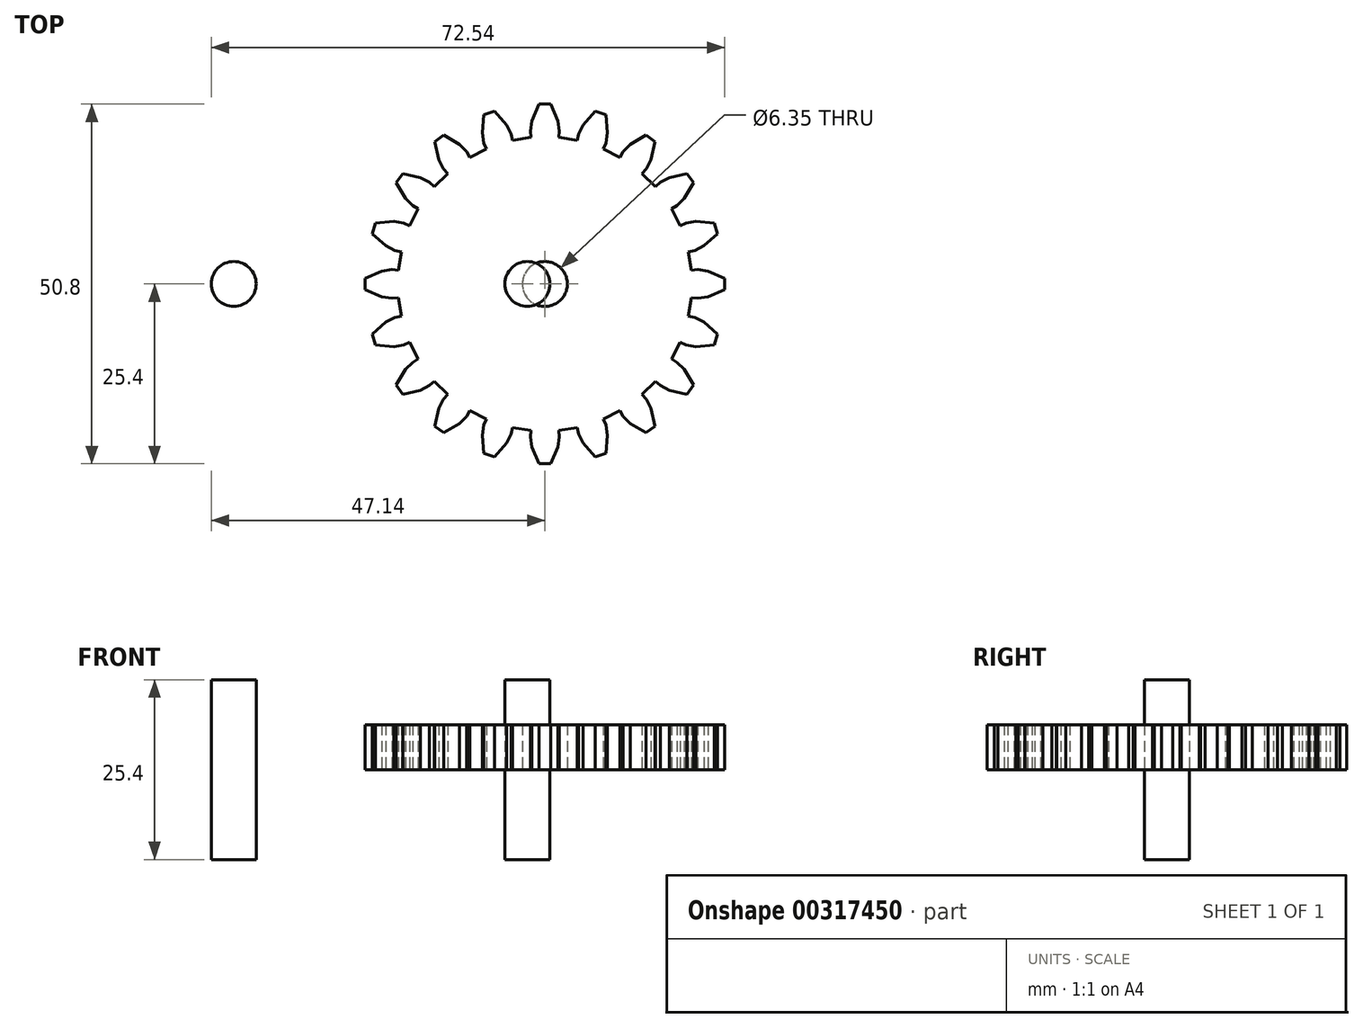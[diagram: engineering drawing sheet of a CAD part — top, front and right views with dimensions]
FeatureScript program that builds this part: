
annotation { "Feature Type Name" : "Feature", "Feature Type Description" : "" }
export const myFeature = defineFeature(function(context is Context, id is Id, definition is map)
    precondition{}
    {
        {
            var Q0;
            Q0=qCreatedBy(makeId("Top.planeOp"),FACE);
            var sketch = newSketch(context, id + "F0", { "sketchPlane" : qUnion([Q0])});
            skLineSegment(sketch, "E0", {"start": v(20.7, 1.94) * mm, "end": v(21.61, 2.03) * mm});
            skLineSegment(sketch, "E1", {"start": v(21.61, 2.03) * mm, "end": v(23.03, 1.81) * mm});
            skLineSegment(sketch, "E2", {"start": v(23.03, 1.81) * mm, "end": v(25.4, 0.8) * mm});
            skLineSegment(sketch, "E3", {"start": v(25.4, 0.8) * mm, "end": v(25.4, -0.8) * mm});
            skLineSegment(sketch, "E4", {"start": v(25.4, -0.8) * mm, "end": v(23.03, -1.81) * mm});
            skLineSegment(sketch, "E5", {"start": v(23.03, -1.81) * mm, "end": v(21.61, -2.03) * mm});
            skLineSegment(sketch, "E6", {"start": v(21.61, -2.03) * mm, "end": v(20.7, -1.94) * mm});
            skLineSegment(sketch, "E7", {"start": v(20.7, -1.94) * mm, "end": v(20.29, -4.55) * mm});
            skLineSegment(sketch, "E8", {"start": v(20.29, -4.55) * mm, "end": v(21.18, -4.75) * mm});
            skLineSegment(sketch, "E9", {"start": v(21.18, -4.75) * mm, "end": v(22.46, -5.4) * mm});
            skLineSegment(sketch, "E10", {"start": v(22.46, -5.4) * mm, "end": v(24.4, -7.09) * mm});
            skLineSegment(sketch, "E11", {"start": v(24.4, -7.09) * mm, "end": v(23.9, -8.61) * mm});
            skLineSegment(sketch, "E12", {"start": v(23.9, -8.61) * mm, "end": v(21.34, -8.84) * mm});
            skLineSegment(sketch, "E13", {"start": v(21.34, -8.84) * mm, "end": v(19.93, -8.6) * mm});
            skLineSegment(sketch, "E14", {"start": v(19.93, -8.6) * mm, "end": v(19.09, -8.24) * mm});
            skLineSegment(sketch, "E15", {"start": v(19.09, -8.24) * mm, "end": v(17.89, -10.6) * mm});
            skLineSegment(sketch, "E16", {"start": v(17.89, -10.6) * mm, "end": v(18.68, -11.07) * mm});
            skLineSegment(sketch, "E17", {"start": v(18.68, -11.07) * mm, "end": v(19.7, -12.07) * mm});
            skLineSegment(sketch, "E18", {"start": v(19.7, -12.07) * mm, "end": v(21.02, -14.28) * mm});
            skLineSegment(sketch, "E19", {"start": v(21.02, -14.28) * mm, "end": v(20.08, -15.58) * mm});
            skLineSegment(sketch, "E20", {"start": v(20.08, -15.58) * mm, "end": v(17.57, -15) * mm});
            skLineSegment(sketch, "E21", {"start": v(17.57, -15) * mm, "end": v(16.3, -14.34) * mm});
            skLineSegment(sketch, "E22", {"start": v(16.3, -14.34) * mm, "end": v(15.6, -13.74) * mm});
            skLineSegment(sketch, "E23", {"start": v(15.6, -13.74) * mm, "end": v(13.74, -15.6) * mm});
            skLineSegment(sketch, "E24", {"start": v(13.74, -15.6) * mm, "end": v(14.34, -16.3) * mm});
            skLineSegment(sketch, "E25", {"start": v(14.34, -16.3) * mm, "end": v(15, -17.57) * mm});
            skLineSegment(sketch, "E26", {"start": v(15, -17.57) * mm, "end": v(15.58, -20.08) * mm});
            skLineSegment(sketch, "E27", {"start": v(15.58, -20.08) * mm, "end": v(14.28, -21.02) * mm});
            skLineSegment(sketch, "E28", {"start": v(14.28, -21.02) * mm, "end": v(12.07, -19.7) * mm});
            skLineSegment(sketch, "E29", {"start": v(12.07, -19.7) * mm, "end": v(11.07, -18.68) * mm});
            skLineSegment(sketch, "E30", {"start": v(11.07, -18.68) * mm, "end": v(10.6, -17.89) * mm});
            skLineSegment(sketch, "E31", {"start": v(10.6, -17.89) * mm, "end": v(8.24, -19.09) * mm});
            skLineSegment(sketch, "E32", {"start": v(8.24, -19.09) * mm, "end": v(8.6, -19.93) * mm});
            skLineSegment(sketch, "E33", {"start": v(8.6, -19.93) * mm, "end": v(8.84, -21.34) * mm});
            skLineSegment(sketch, "E34", {"start": v(8.84, -21.34) * mm, "end": v(8.61, -23.9) * mm});
            skLineSegment(sketch, "E35", {"start": v(8.61, -23.9) * mm, "end": v(7.09, -24.4) * mm});
            skLineSegment(sketch, "E36", {"start": v(7.09, -24.4) * mm, "end": v(5.4, -22.46) * mm});
            skLineSegment(sketch, "E37", {"start": v(5.4, -22.46) * mm, "end": v(4.75, -21.18) * mm});
            skLineSegment(sketch, "E38", {"start": v(4.75, -21.18) * mm, "end": v(4.55, -20.29) * mm});
            skLineSegment(sketch, "E39", {"start": v(4.55, -20.29) * mm, "end": v(1.94, -20.7) * mm});
            skLineSegment(sketch, "E40", {"start": v(1.94, -20.7) * mm, "end": v(2.03, -21.61) * mm});
            skLineSegment(sketch, "E41", {"start": v(2.03, -21.61) * mm, "end": v(1.81, -23.03) * mm});
            skLineSegment(sketch, "E42", {"start": v(1.81, -23.03) * mm, "end": v(0.8, -25.4) * mm});
            skLineSegment(sketch, "E43", {"start": v(0.8, -25.4) * mm, "end": v(-0.8, -25.4) * mm});
            skLineSegment(sketch, "E44", {"start": v(-0.8, -25.4) * mm, "end": v(-1.81, -23.03) * mm});
            skLineSegment(sketch, "E45", {"start": v(-1.81, -23.03) * mm, "end": v(-2.03, -21.61) * mm});
            skLineSegment(sketch, "E46", {"start": v(-2.03, -21.61) * mm, "end": v(-1.94, -20.7) * mm});
            skLineSegment(sketch, "E47", {"start": v(-1.94, -20.7) * mm, "end": v(-4.55, -20.29) * mm});
            skLineSegment(sketch, "E48", {"start": v(-4.55, -20.29) * mm, "end": v(-4.75, -21.18) * mm});
            skLineSegment(sketch, "E49", {"start": v(-4.75, -21.18) * mm, "end": v(-5.4, -22.46) * mm});
            skLineSegment(sketch, "E50", {"start": v(-5.4, -22.46) * mm, "end": v(-7.09, -24.4) * mm});
            skLineSegment(sketch, "E51", {"start": v(-7.09, -24.4) * mm, "end": v(-8.61, -23.9) * mm});
            skLineSegment(sketch, "E52", {"start": v(-8.61, -23.9) * mm, "end": v(-8.84, -21.34) * mm});
            skLineSegment(sketch, "E53", {"start": v(-8.84, -21.34) * mm, "end": v(-8.6, -19.93) * mm});
            skLineSegment(sketch, "E54", {"start": v(-8.6, -19.93) * mm, "end": v(-8.24, -19.09) * mm});
            skLineSegment(sketch, "E55", {"start": v(-8.24, -19.09) * mm, "end": v(-10.6, -17.89) * mm});
            skLineSegment(sketch, "E56", {"start": v(-10.6, -17.89) * mm, "end": v(-11.07, -18.68) * mm});
            skLineSegment(sketch, "E57", {"start": v(-11.07, -18.68) * mm, "end": v(-12.07, -19.7) * mm});
            skLineSegment(sketch, "E58", {"start": v(-12.07, -19.7) * mm, "end": v(-14.28, -21.02) * mm});
            skLineSegment(sketch, "E59", {"start": v(-14.28, -21.02) * mm, "end": v(-15.58, -20.08) * mm});
            skLineSegment(sketch, "E60", {"start": v(-15.58, -20.08) * mm, "end": v(-15, -17.57) * mm});
            skLineSegment(sketch, "E61", {"start": v(-15, -17.57) * mm, "end": v(-14.34, -16.3) * mm});
            skLineSegment(sketch, "E62", {"start": v(-14.34, -16.3) * mm, "end": v(-13.74, -15.6) * mm});
            skLineSegment(sketch, "E63", {"start": v(-13.74, -15.6) * mm, "end": v(-15.6, -13.74) * mm});
            skLineSegment(sketch, "E64", {"start": v(-15.6, -13.74) * mm, "end": v(-16.3, -14.34) * mm});
            skLineSegment(sketch, "E65", {"start": v(-16.3, -14.34) * mm, "end": v(-17.57, -15) * mm});
            skLineSegment(sketch, "E66", {"start": v(-17.57, -15) * mm, "end": v(-20.08, -15.58) * mm});
            skLineSegment(sketch, "E67", {"start": v(-20.08, -15.58) * mm, "end": v(-21.02, -14.28) * mm});
            skLineSegment(sketch, "E68", {"start": v(-21.02, -14.28) * mm, "end": v(-19.7, -12.07) * mm});
            skLineSegment(sketch, "E69", {"start": v(-19.7, -12.07) * mm, "end": v(-18.68, -11.07) * mm});
            skLineSegment(sketch, "E70", {"start": v(-18.68, -11.07) * mm, "end": v(-17.89, -10.6) * mm});
            skLineSegment(sketch, "E71", {"start": v(-17.89, -10.6) * mm, "end": v(-19.09, -8.24) * mm});
            skLineSegment(sketch, "E72", {"start": v(-19.09, -8.24) * mm, "end": v(-19.93, -8.6) * mm});
            skLineSegment(sketch, "E73", {"start": v(-19.93, -8.6) * mm, "end": v(-21.34, -8.84) * mm});
            skLineSegment(sketch, "E74", {"start": v(-21.34, -8.84) * mm, "end": v(-23.9, -8.61) * mm});
            skLineSegment(sketch, "E75", {"start": v(-23.9, -8.61) * mm, "end": v(-24.4, -7.09) * mm});
            skLineSegment(sketch, "E76", {"start": v(-24.4, -7.09) * mm, "end": v(-22.46, -5.4) * mm});
            skLineSegment(sketch, "E77", {"start": v(-22.46, -5.4) * mm, "end": v(-21.18, -4.75) * mm});
            skLineSegment(sketch, "E78", {"start": v(-21.18, -4.75) * mm, "end": v(-20.29, -4.55) * mm});
            skLineSegment(sketch, "E79", {"start": v(-20.29, -4.55) * mm, "end": v(-20.7, -1.94) * mm});
            skLineSegment(sketch, "E80", {"start": v(-20.7, -1.94) * mm, "end": v(-21.61, -2.03) * mm});
            skLineSegment(sketch, "E81", {"start": v(-21.61, -2.03) * mm, "end": v(-23.03, -1.81) * mm});
            skLineSegment(sketch, "E82", {"start": v(-23.03, -1.81) * mm, "end": v(-25.4, -0.8) * mm});
            skLineSegment(sketch, "E83", {"start": v(-25.4, -0.8) * mm, "end": v(-25.4, 0.8) * mm});
            skLineSegment(sketch, "E84", {"start": v(-25.4, 0.8) * mm, "end": v(-23.03, 1.81) * mm});
            skLineSegment(sketch, "E85", {"start": v(-23.03, 1.81) * mm, "end": v(-21.61, 2.03) * mm});
            skLineSegment(sketch, "E86", {"start": v(-21.61, 2.03) * mm, "end": v(-20.7, 1.94) * mm});
            skLineSegment(sketch, "E87", {"start": v(-20.7, 1.94) * mm, "end": v(-20.29, 4.55) * mm});
            skLineSegment(sketch, "E88", {"start": v(-20.29, 4.55) * mm, "end": v(-21.18, 4.75) * mm});
            skLineSegment(sketch, "E89", {"start": v(-21.18, 4.75) * mm, "end": v(-22.46, 5.4) * mm});
            skLineSegment(sketch, "E90", {"start": v(-22.46, 5.4) * mm, "end": v(-24.4, 7.09) * mm});
            skLineSegment(sketch, "E91", {"start": v(-24.4, 7.09) * mm, "end": v(-23.9, 8.61) * mm});
            skLineSegment(sketch, "E92", {"start": v(-23.9, 8.61) * mm, "end": v(-21.34, 8.84) * mm});
            skLineSegment(sketch, "E93", {"start": v(-21.34, 8.84) * mm, "end": v(-19.93, 8.6) * mm});
            skLineSegment(sketch, "E94", {"start": v(-19.93, 8.6) * mm, "end": v(-19.09, 8.24) * mm});
            skLineSegment(sketch, "E95", {"start": v(-19.09, 8.24) * mm, "end": v(-17.89, 10.6) * mm});
            skLineSegment(sketch, "E96", {"start": v(-17.89, 10.6) * mm, "end": v(-18.68, 11.07) * mm});
            skLineSegment(sketch, "E97", {"start": v(-18.68, 11.07) * mm, "end": v(-19.7, 12.07) * mm});
            skLineSegment(sketch, "E98", {"start": v(-19.7, 12.07) * mm, "end": v(-21.02, 14.28) * mm});
            skLineSegment(sketch, "E99", {"start": v(-21.02, 14.28) * mm, "end": v(-20.08, 15.58) * mm});
            skLineSegment(sketch, "E100", {"start": v(-20.08, 15.58) * mm, "end": v(-17.57, 15) * mm});
            skLineSegment(sketch, "E101", {"start": v(-17.57, 15) * mm, "end": v(-16.3, 14.34) * mm});
            skLineSegment(sketch, "E102", {"start": v(-16.3, 14.34) * mm, "end": v(-15.6, 13.74) * mm});
            skLineSegment(sketch, "E103", {"start": v(-15.6, 13.74) * mm, "end": v(-13.74, 15.6) * mm});
            skLineSegment(sketch, "E104", {"start": v(-13.74, 15.6) * mm, "end": v(-14.34, 16.3) * mm});
            skLineSegment(sketch, "E105", {"start": v(-14.34, 16.3) * mm, "end": v(-15, 17.57) * mm});
            skLineSegment(sketch, "E106", {"start": v(-15, 17.57) * mm, "end": v(-15.58, 20.08) * mm});
            skLineSegment(sketch, "E107", {"start": v(-15.58, 20.08) * mm, "end": v(-14.28, 21.02) * mm});
            skLineSegment(sketch, "E108", {"start": v(-14.28, 21.02) * mm, "end": v(-12.07, 19.7) * mm});
            skLineSegment(sketch, "E109", {"start": v(-12.07, 19.7) * mm, "end": v(-11.07, 18.68) * mm});
            skLineSegment(sketch, "E110", {"start": v(-11.07, 18.68) * mm, "end": v(-10.6, 17.89) * mm});
            skLineSegment(sketch, "E111", {"start": v(-10.6, 17.89) * mm, "end": v(-8.24, 19.09) * mm});
            skLineSegment(sketch, "E112", {"start": v(-8.24, 19.09) * mm, "end": v(-8.6, 19.93) * mm});
            skLineSegment(sketch, "E113", {"start": v(-8.6, 19.93) * mm, "end": v(-8.84, 21.34) * mm});
            skLineSegment(sketch, "E114", {"start": v(-8.84, 21.34) * mm, "end": v(-8.61, 23.9) * mm});
            skLineSegment(sketch, "E115", {"start": v(-8.61, 23.9) * mm, "end": v(-7.09, 24.4) * mm});
            skLineSegment(sketch, "E116", {"start": v(-7.09, 24.4) * mm, "end": v(-5.4, 22.46) * mm});
            skLineSegment(sketch, "E117", {"start": v(-5.4, 22.46) * mm, "end": v(-4.75, 21.18) * mm});
            skLineSegment(sketch, "E118", {"start": v(-4.75, 21.18) * mm, "end": v(-4.55, 20.29) * mm});
            skLineSegment(sketch, "E119", {"start": v(-4.55, 20.29) * mm, "end": v(-1.94, 20.7) * mm});
            skLineSegment(sketch, "E120", {"start": v(-1.94, 20.7) * mm, "end": v(-2.03, 21.61) * mm});
            skLineSegment(sketch, "E121", {"start": v(-2.03, 21.61) * mm, "end": v(-1.81, 23.03) * mm});
            skLineSegment(sketch, "E122", {"start": v(-1.81, 23.03) * mm, "end": v(-0.8, 25.4) * mm});
            skLineSegment(sketch, "E123", {"start": v(-0.8, 25.4) * mm, "end": v(0.8, 25.4) * mm});
            skLineSegment(sketch, "E124", {"start": v(0.8, 25.4) * mm, "end": v(1.81, 23.03) * mm});
            skLineSegment(sketch, "E125", {"start": v(1.81, 23.03) * mm, "end": v(2.03, 21.61) * mm});
            skLineSegment(sketch, "E126", {"start": v(2.03, 21.61) * mm, "end": v(1.94, 20.7) * mm});
            skLineSegment(sketch, "E127", {"start": v(1.94, 20.7) * mm, "end": v(4.55, 20.29) * mm});
            skLineSegment(sketch, "E128", {"start": v(4.55, 20.29) * mm, "end": v(4.75, 21.18) * mm});
            skLineSegment(sketch, "E129", {"start": v(4.75, 21.18) * mm, "end": v(5.4, 22.46) * mm});
            skLineSegment(sketch, "E130", {"start": v(5.4, 22.46) * mm, "end": v(7.09, 24.4) * mm});
            skLineSegment(sketch, "E131", {"start": v(7.09, 24.4) * mm, "end": v(8.61, 23.9) * mm});
            skLineSegment(sketch, "E132", {"start": v(8.61, 23.9) * mm, "end": v(8.84, 21.34) * mm});
            skLineSegment(sketch, "E133", {"start": v(8.84, 21.34) * mm, "end": v(8.6, 19.93) * mm});
            skLineSegment(sketch, "E134", {"start": v(8.6, 19.93) * mm, "end": v(8.24, 19.09) * mm});
            skLineSegment(sketch, "E135", {"start": v(8.24, 19.09) * mm, "end": v(10.6, 17.89) * mm});
            skLineSegment(sketch, "E136", {"start": v(10.6, 17.89) * mm, "end": v(11.07, 18.68) * mm});
            skLineSegment(sketch, "E137", {"start": v(11.07, 18.68) * mm, "end": v(12.07, 19.7) * mm});
            skLineSegment(sketch, "E138", {"start": v(12.07, 19.7) * mm, "end": v(14.28, 21.02) * mm});
            skLineSegment(sketch, "E139", {"start": v(14.28, 21.02) * mm, "end": v(15.58, 20.08) * mm});
            skLineSegment(sketch, "E140", {"start": v(15.58, 20.08) * mm, "end": v(15, 17.57) * mm});
            skLineSegment(sketch, "E141", {"start": v(15, 17.57) * mm, "end": v(14.34, 16.3) * mm});
            skLineSegment(sketch, "E142", {"start": v(14.34, 16.3) * mm, "end": v(13.74, 15.6) * mm});
            skLineSegment(sketch, "E143", {"start": v(13.74, 15.6) * mm, "end": v(15.6, 13.74) * mm});
            skLineSegment(sketch, "E144", {"start": v(15.6, 13.74) * mm, "end": v(16.3, 14.34) * mm});
            skLineSegment(sketch, "E145", {"start": v(16.3, 14.34) * mm, "end": v(17.57, 15) * mm});
            skLineSegment(sketch, "E146", {"start": v(17.57, 15) * mm, "end": v(20.08, 15.58) * mm});
            skLineSegment(sketch, "E147", {"start": v(20.08, 15.58) * mm, "end": v(21.02, 14.28) * mm});
            skLineSegment(sketch, "E148", {"start": v(21.02, 14.28) * mm, "end": v(19.7, 12.07) * mm});
            skLineSegment(sketch, "E149", {"start": v(19.7, 12.07) * mm, "end": v(18.68, 11.07) * mm});
            skLineSegment(sketch, "E150", {"start": v(18.68, 11.07) * mm, "end": v(17.89, 10.6) * mm});
            skLineSegment(sketch, "E151", {"start": v(17.89, 10.6) * mm, "end": v(19.09, 8.24) * mm});
            skLineSegment(sketch, "E152", {"start": v(19.09, 8.24) * mm, "end": v(19.93, 8.6) * mm});
            skLineSegment(sketch, "E153", {"start": v(19.93, 8.6) * mm, "end": v(21.34, 8.84) * mm});
            skLineSegment(sketch, "E154", {"start": v(21.34, 8.84) * mm, "end": v(23.9, 8.61) * mm});
            skLineSegment(sketch, "E155", {"start": v(23.9, 8.61) * mm, "end": v(24.4, 7.09) * mm});
            skLineSegment(sketch, "E156", {"start": v(24.4, 7.09) * mm, "end": v(22.46, 5.4) * mm});
            skLineSegment(sketch, "E157", {"start": v(22.46, 5.4) * mm, "end": v(21.18, 4.75) * mm});
            skLineSegment(sketch, "E158", {"start": v(21.18, 4.75) * mm, "end": v(20.29, 4.55) * mm});
            skLineSegment(sketch, "E159", {"start": v(20.29, 4.55) * mm, "end": v(20.7, 1.94) * mm});
            skCircle(sketch, "E160", {"center": v(0, 0) * mm, "radius": 3.18 * mm});
            skSolve(sketch);
        }
        {
            var Q0;
            Q0=makeQuery(id+"F0.imprint","IMPRINT",FACE,{"disambiguationData":[TD([[makeQuery(id+"F0.imprint","IMPRINT",EDGE,{"derivedFrom":sQuery(id+"F0.wireOp",EDGE,"E0")}),-1.0]])]});
            extrude(context, id + "F1", {"entities" : qUnion([Q0]), "depth" : 6.35 * mm});
        }
        {
            var Q0;
            Q0=qCreatedBy(makeId("Top.planeOp"),FACE);
            var sketch = newSketch(context, id + "F2", { "sketchPlane" : qUnion([Q0])});
            skCircle(sketch, "E161", {"center": v(-43.96, 0) * mm, "radius": 3.18 * mm});
            skCircle(sketch, "E162", {"center": v(-2.46, 0) * mm, "radius": 3.18 * mm});
            skSolve(sketch);
        }
        {
            var Q0;
            Q0=makeQuery(id+"F2.imprint","IMPRINT",FACE,{"disambiguationData":[TD([[makeQuery(id+"F2.imprint","IMPRINT",EDGE,{"derivedFrom":sQuery(id+"F2.wireOp",EDGE,"E161")}),1.0]])]});
            var Q1;
            Q1=makeQuery(id+"F2.imprint","IMPRINT",FACE,{"disambiguationData":[TD([[makeQuery(id+"F2.imprint","IMPRINT",EDGE,{"derivedFrom":sQuery(id+"F2.wireOp",EDGE,"E162")}),1.0]])]});
            extrude(context, id + "F3", {"entities" : qUnion([Q0, Q1]), "depth" : 12.7 * mm, "hasSecondDirection" : true, "secondDirectionOppositeDirection" : true, "secondDirectionDepth" : 12.7 * mm});
        }
    });
